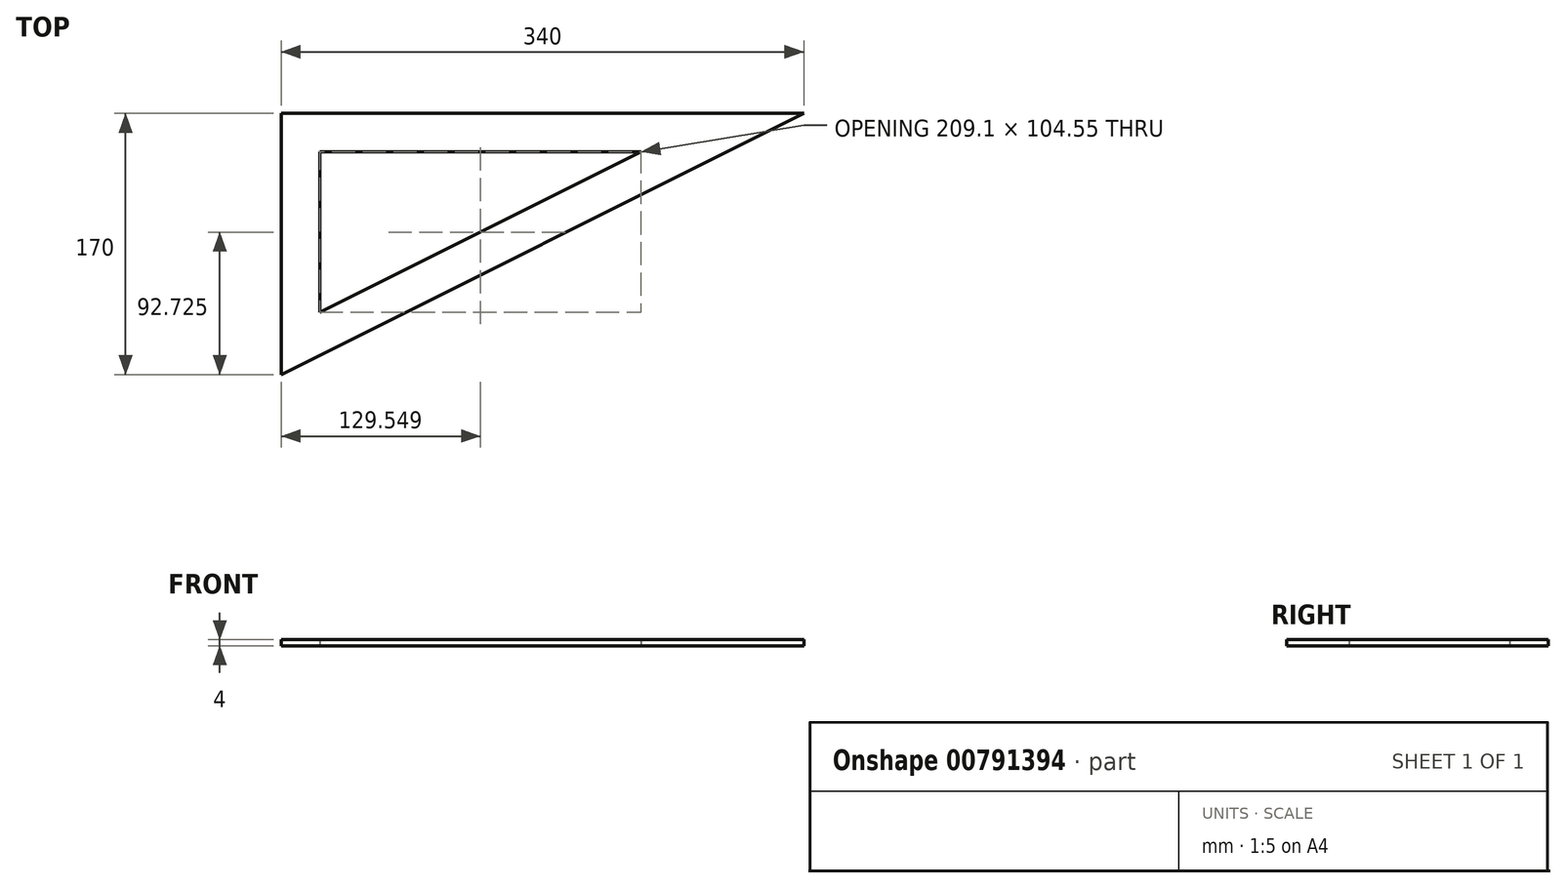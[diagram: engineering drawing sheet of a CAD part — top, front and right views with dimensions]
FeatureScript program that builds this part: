
annotation { "Feature Type Name" : "Feature", "Feature Type Description" : "" }
export const myFeature = defineFeature(function(context is Context, id is Id, definition is map)
    precondition{}
    {
        {
            var Q0;
            Q0=qCreatedBy(makeId("Top.planeOp"),FACE);
            var sketch = newSketch(context, id + "F0", { "sketchPlane" : qUnion([Q0])});
            skLineSegment(sketch, "E0", {"start": v(-170, 85) * mm, "end": v(-170, -85) * mm});
            skLineSegment(sketch, "E1", {"start": v(-170, -85) * mm, "end": v(170, 85) * mm});
            skLineSegment(sketch, "E2", {"start": v(170, 85) * mm, "end": v(-170, 85) * mm});
            skLineSegment(sketch, "E3.0", {"start": v(-145, 60) * mm, "end": v(-145, -44.55) * mm});
            skLineSegment(sketch, "E3.1", {"start": v(64.1, 60) * mm, "end": v(-145, 60) * mm});
            skLineSegment(sketch, "E3.2", {"start": v(-145, -44.55) * mm, "end": v(64.1, 60) * mm});
            skSolve(sketch);
        }
        {
            var Q0;
            Q0 = qSketchRegion(id + "F0", true);
            extrude(context, id + "F1", {"entities" : qUnion([Q0]), "depth" : 4 * mm, "offsetDistance" : 25 * mm, "symmetric" : true});
        }
    });
